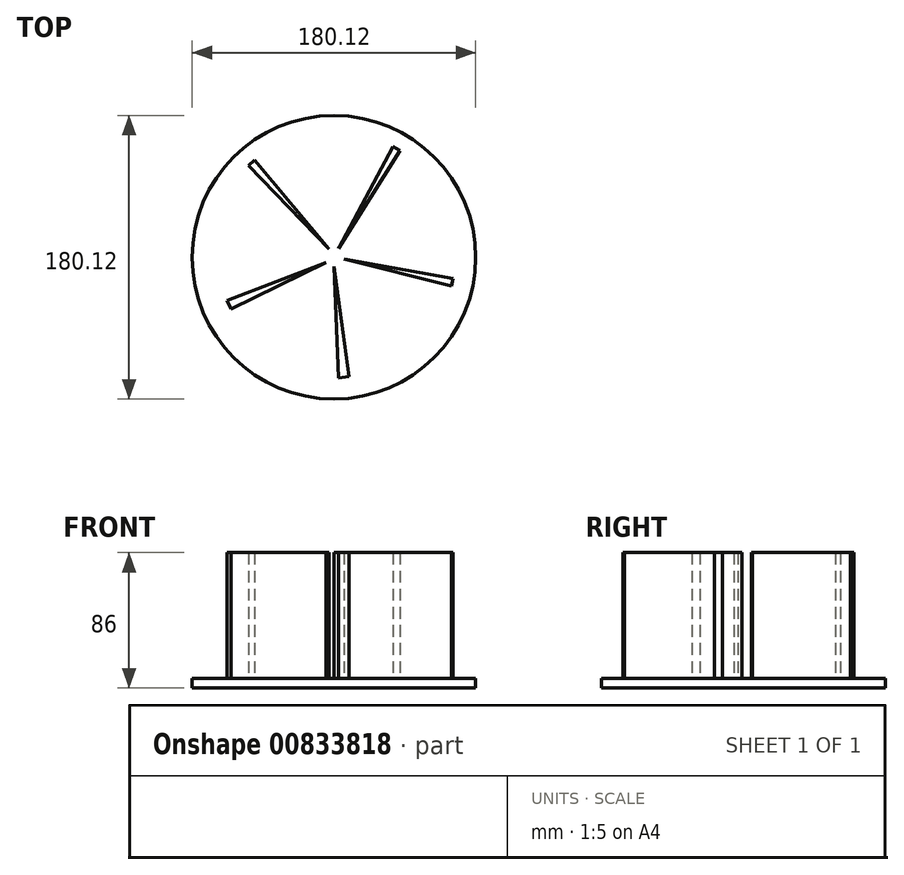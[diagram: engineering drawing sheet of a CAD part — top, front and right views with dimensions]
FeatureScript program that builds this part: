
annotation { "Feature Type Name" : "Feature", "Feature Type Description" : "" }
export const myFeature = defineFeature(function(context is Context, id is Id, definition is map)
    precondition{}
    {
        {
            var Q0;
            Q0=qCreatedBy(makeId("Top.planeOp"),FACE);
            var sketch = newSketch(context, id + "F0", { "sketchPlane" : qUnion([Q0])});
            skCircle(sketch, "E0", {"center": v(0, 0) * mm, "radius": 90.06 * mm});
            skSolve(sketch);
        }
        {
            var Q0;
            Q0 = qSketchRegion(id + "F0", true);
            extrude(context, id + "F1", {"entities" : qUnion([Q0]), "depth" : 6 * mm, "offsetDistance" : 25 * mm});
        }
        {
            var Q0;
            Q0=makeQuery(id+"F1.opExtrude","CAP_FACE",FACE,{"disambiguationData":[OSD([sQuery(id+"F0.wireOp",EDGE,"E0")])],"isStart":false});
            var sketch = newSketch(context, id + "F2", { "sketchPlane" : qUnion([Q0])});
            skLineSegment(sketch, "E1", {"start": v(37.47, 70.26) * mm, "end": v(3.05, 5.71) * mm});
            skLineSegment(sketch, "E2", {"start": v(6.37, -1.13) * mm, "end": v(75.55, -13.42) * mm});
            skPoint(sketch, "E3.visualSharp", {"position": v(0, 0) * mm});
            skLineSegment(sketch, "E4", {"start": v(0, -6) * mm, "end": v(9.7, -75.67) * mm});
            skLineSegment(sketch, "E5", {"start": v(-3.06, 5.16) * mm, "end": v(-54.17, 58.23) * mm});
            skLineSegment(sketch, "E6", {"start": v(-4.9, -3.45) * mm, "end": v(-65.31, -32.81) * mm});
            skLineSegment(sketch, "E7", {"start": v(-54.17, 58.23) * mm, "end": v(-50.56, 61.7) * mm});
            skLineSegment(sketch, "E8", {"start": v(-50.56, 61.7) * mm, "end": v(-3.06, 5.16) * mm});
            skLineSegment(sketch, "E9", {"start": v(37.47, 70.26) * mm, "end": v(41.9, 67.9) * mm});
            skLineSegment(sketch, "E10", {"start": v(41.9, 67.9) * mm, "end": v(3.05, 5.71) * mm});
            skLineSegment(sketch, "E11", {"start": v(75.55, -13.42) * mm, "end": v(74.67, -18.35) * mm});
            skLineSegment(sketch, "E12", {"start": v(74.67, -18.35) * mm, "end": v(6.37, -1.13) * mm});
            skLineSegment(sketch, "E13", {"start": v(9.7, -75.67) * mm, "end": v(3.05, -76.6) * mm});
            skLineSegment(sketch, "E14", {"start": v(3.05, -76.6) * mm, "end": v(0, -6) * mm});
            skLineSegment(sketch, "E15", {"start": v(-65.31, -32.81) * mm, "end": v(-67.9, -27.49) * mm});
            skLineSegment(sketch, "E16", {"start": v(-67.9, -27.49) * mm, "end": v(-4.9, -3.45) * mm});
            skSolve(sketch);
        }
        {
            var Q0;
            Q0 = qSketchRegion(id + "F2", true);
            extrude(context, id + "F3", {"entities" : qUnion([Q0]), "operationType" : NewBodyOperationType.ADD, "depth" : 80 * mm, "offsetDistance" : 25 * mm});
        }
    });
